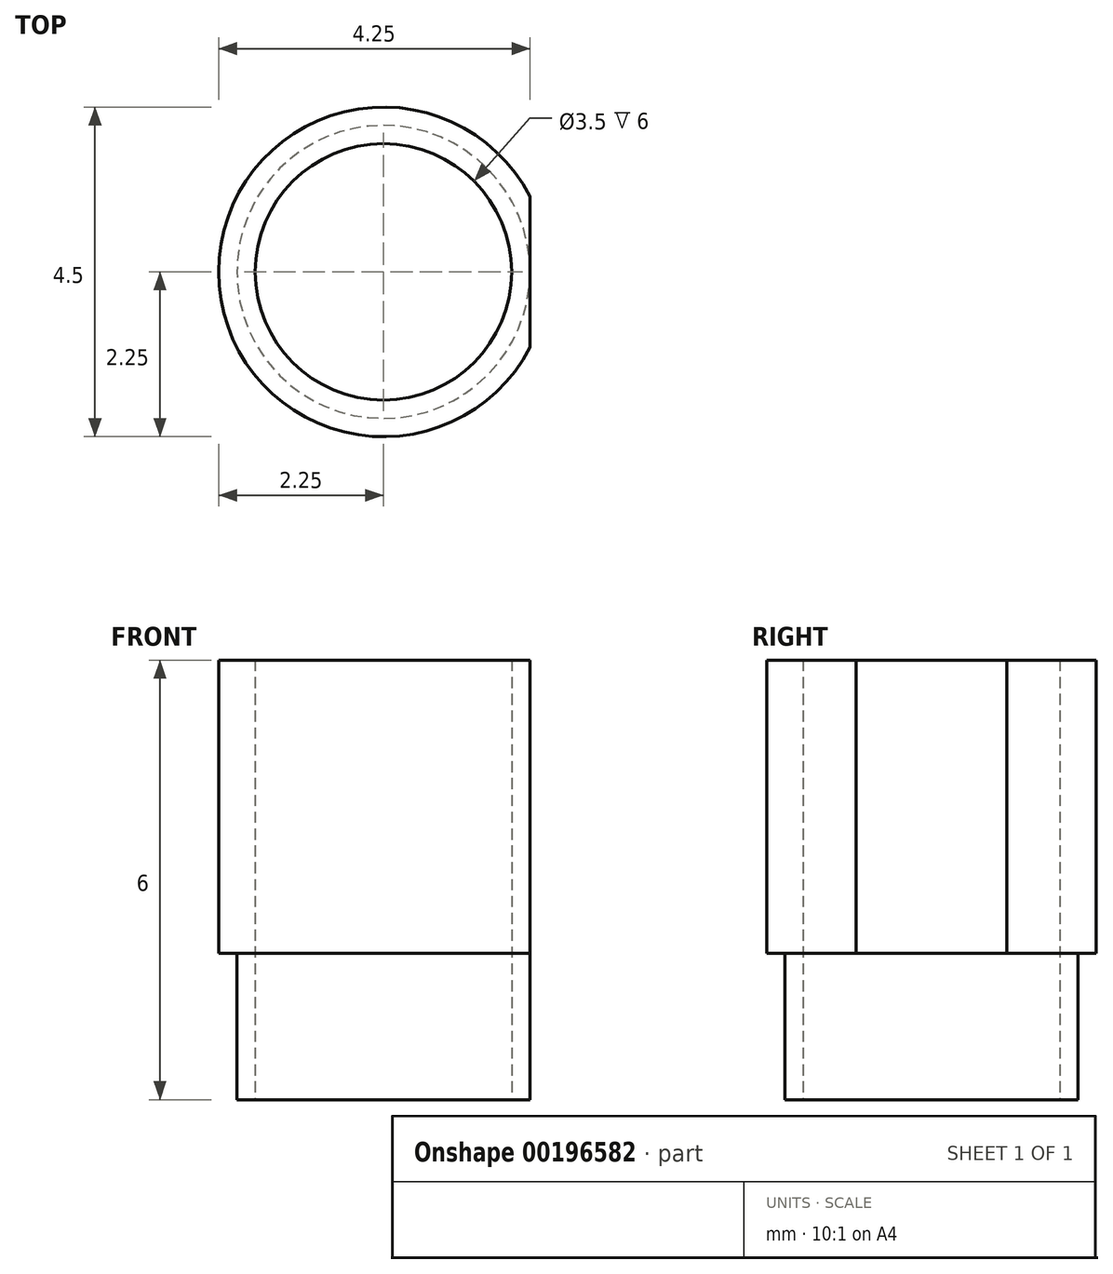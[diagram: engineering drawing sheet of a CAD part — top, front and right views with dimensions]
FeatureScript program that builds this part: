
annotation { "Feature Type Name" : "Feature", "Feature Type Description" : "" }
export const myFeature = defineFeature(function(context is Context, id is Id, definition is map)
    precondition{}
    {
        {
            var Q0;
            Q0=qCreatedBy(makeId("Top.planeOp"),FACE);
            var sketch = newSketch(context, id + "F0", { "sketchPlane" : qUnion([Q0])});
            skCircle(sketch, "E0", {"center": v(0, 0) * mm, "radius": 1.75 * mm});
            skArc(sketch, "E1", {"start": v(2, 1.03) * mm, "mid": v(-2.25, 0) * mm, "end": v(2, -1.03) * mm});
            skLineSegment(sketch, "E2", {"start": v(2, 1.03) * mm, "end": v(2, -1.03) * mm});
            skCircle(sketch, "E3", {"center": v(0, 0) * mm, "radius": 2 * mm});
            skSolve(sketch);
        }
        {
            var Q0;
            Q0=makeQuery(id+"F0.imprint","IMPRINT",FACE,{"disambiguationData":[TD([[makeQuery(id+"F0.imprint","IMPRINT",EDGE,{"derivedFrom":sQuery(id+"F0.wireOp",EDGE,"E0")}),-1.0]])]});
            var Q1;
            {var subQ0=sQuery(id+"F0.wireOp",EDGE,"E1");Q1=makeQuery(id+"F0.imprint","IMPRINT",FACE,{"disambiguationData":[TD([[makeQuery(id+"F0.imprint","IMPRINT",EDGE,{"derivedFrom":subQ0}),1.0]])]});}
            extrude(context, id + "F1", {"entities" : qUnion([Q0, Q1]), "depth" : 4 * mm});
        }
        {
            var Q0;
            Q0=makeQuery(id+"F0.imprint","IMPRINT",FACE,{"disambiguationData":[TD([[makeQuery(id+"F0.imprint","IMPRINT",EDGE,{"derivedFrom":sQuery(id+"F0.wireOp",EDGE,"E0")}),-1.0]])]});
            extrude(context, id + "F2", {"entities" : qUnion([Q0]), "operationType" : NewBodyOperationType.ADD, "oppositeDirection" : true, "depth" : 2 * mm});
        }
    });
